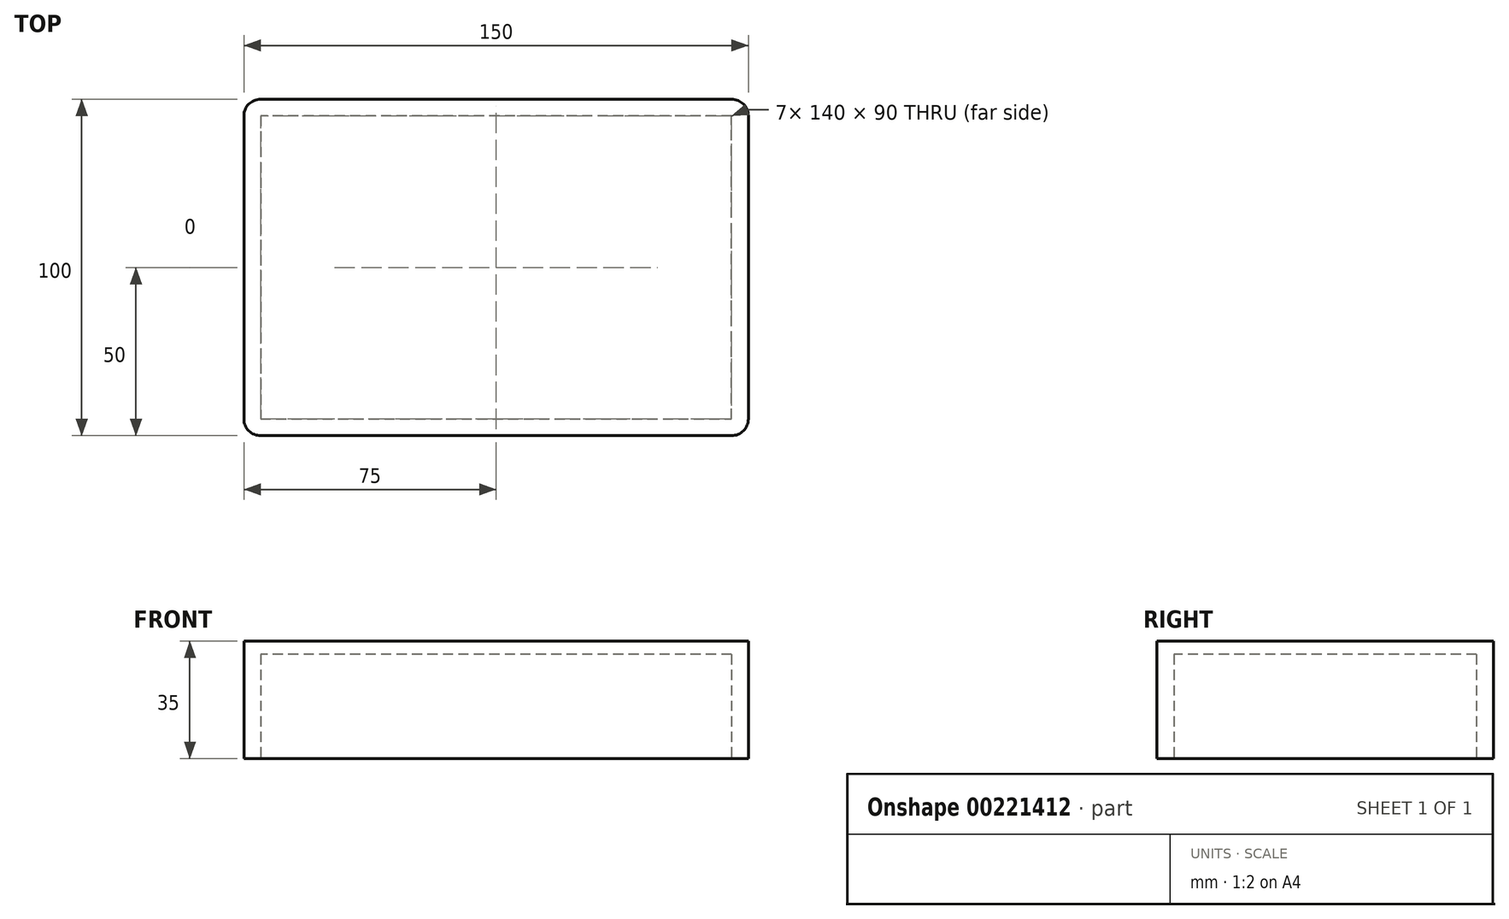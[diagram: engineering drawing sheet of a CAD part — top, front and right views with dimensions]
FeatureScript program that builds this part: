
annotation { "Feature Type Name" : "Feature", "Feature Type Description" : "" }
export const myFeature = defineFeature(function(context is Context, id is Id, definition is map)
    precondition{}
    {
        {
            var Q0;
            Q0=qCreatedBy(makeId("Top.planeOp"),FACE);
            var sketch = newSketch(context, id + "F0", { "sketchPlane" : qUnion([Q0])});
            skLineSegment(sketch, "E0", {"start": v(0, 0) * mm, "end": v(-150, 0) * mm});
            skLineSegment(sketch, "E1", {"start": v(-150, 0) * mm, "end": v(-150, 100) * mm});
            skLineSegment(sketch, "E2", {"start": v(-150, 100) * mm, "end": v(0, 100) * mm});
            skLineSegment(sketch, "E3", {"start": v(0, 100) * mm, "end": v(0, 0) * mm});
            skLineSegment(sketch, "E4", {"start": v(-150, 100) * mm, "end": v(-145, 100) * mm});
            skLineSegment(sketch, "E5", {"start": v(-145, 100) * mm, "end": v(-145, 0) * mm});
            skLineSegment(sketch, "E6", {"start": v(-145, 0) * mm, "end": v(-145, 5) * mm});
            skLineSegment(sketch, "E7", {"start": v(-145, 5) * mm, "end": v(0, 5) * mm});
            skLineSegment(sketch, "E8", {"start": v(0, 5) * mm, "end": v(-5, 5) * mm});
            skLineSegment(sketch, "E9", {"start": v(-5, 5) * mm, "end": v(-5, 100) * mm});
            skLineSegment(sketch, "E10", {"start": v(-5, 100) * mm, "end": v(-5, 95) * mm});
            skLineSegment(sketch, "E11", {"start": v(-5, 95) * mm, "end": v(-145, 95) * mm});
            skSolve(sketch);
        }
        {
            var Q0;
            Q0 = qSketchRegion(id + "F0", true);
            var Q1;
            {var subQ0=sQuery(id+"F0.wireOp",EDGE,"E7");Q1=makeQuery(id+"F0.imprint","IMPRINT",FACE,{"disambiguationData":[TD([[makeQuery(id+"F0.imprint","IMPRINT",EDGE,{"derivedFrom":subQ0}),1.0]])]});}
            extrude(context, id + "F1", {"entities" : qUnion([Q0, Q1]), "depth" : 35 * mm});
        }
        {
            var Q0;
            {var subQ0=sQuery(id+"F0.wireOp",EDGE,"E7");Q0=makeQuery(id+"F0.imprint","IMPRINT",FACE,{"disambiguationData":[TD([[makeQuery(id+"F0.imprint","IMPRINT",EDGE,{"derivedFrom":subQ0}),1.0]])]});}
            extrude(context, id + "F2", {"entities" : qUnion([Q0]), "operationType" : NewBodyOperationType.REMOVE, "depth" : 31 * mm});
        }
        {
            var Q0;
            Q0=makeQuery(id+"F1.opExtrude","SWEPT_EDGE",EDGE,{"disambiguationData":[OSD([sQuery(id+"F0.wireOp",EDGE,"E0"),sQuery(id+"F0.wireOp",EDGE,"E3")])]});
            var Q1;
            Q1=makeQuery(id+"F1.opExtrude","SWEPT_EDGE",EDGE,{"disambiguationData":[OSD([sQuery(id+"F0.wireOp",EDGE,"E2"),sQuery(id+"F0.wireOp",EDGE,"E3")])]});
            var Q2;
            Q2=makeQuery(id+"F1.opExtrude","SWEPT_EDGE",EDGE,{"disambiguationData":[OSD([sQuery(id+"F0.wireOp",EDGE,"E1"),sQuery(id+"F0.wireOp",EDGE,"E4")])]});
            var Q3;
            Q3=makeQuery(id+"F1.opExtrude","SWEPT_EDGE",EDGE,{"disambiguationData":[OSD([sQuery(id+"F0.wireOp",EDGE,"E0"),sQuery(id+"F0.wireOp",EDGE,"E1")])]});
            fillet(context, id + "F3", {"entities" : qUnion([Q0, Q1, Q2, Q3]), "radius" : 5 * mm, "tangentPropagation" : true, "allowEdgeOverflow" : false});
        }
    });
